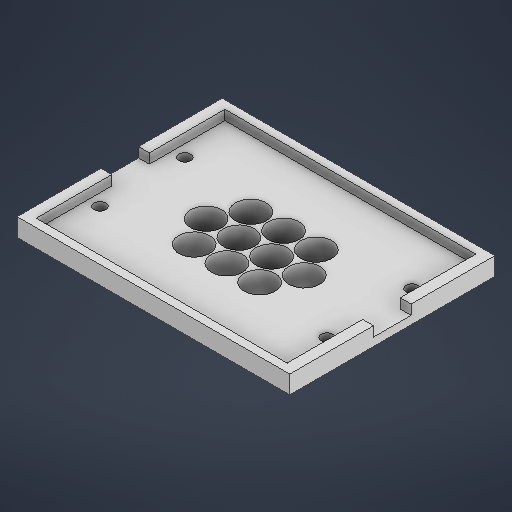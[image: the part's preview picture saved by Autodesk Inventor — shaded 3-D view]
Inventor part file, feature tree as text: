
AUTODESK INVENTOR PART (.ipt)
format: ipt  version: 2025.2 (Build 292293000, 293)  size: 641,024 bytes
history: native  units: mm
features: extrude x5, sketch x5, projected_geometry x4
ambient origin geometry x8: Origin, YZ Plane, XZ Plane, XY Plane, X Axis, Y Axis, Z Axis, Center Point
bodies: Solid1 (feature_tree)
feature tree (14):
  extrude  "Extrusion1"  Depth=19.0mm
  sketch  "Sketch4"  dims[d4=19.0mm d6=19.0mm]
  extrude  "Extrusion7"  Depth=19.0mm
  sketch  "Sketch5"  dims[d8=19.0mm d10=19.0mm]
  extrude  "Extrusion8"  Depth=19.0mm
  extrude  "Extrusion6"  Depth=19.0mm
  extrude  "Extrusion9"  Depth=15.0mm TaperAngle=0.0deg
  sketch  "Sketch1"  dims[d0=19.0mm d2=19.0mm]
  projected_geometry  "Projected Loop1"
  sketch  "Sketch6"  dims[d11=19.0mm d13=19.0mm]
  projected_geometry  "Projected Loop4"
  sketch  "Sketch7"  dims[d14=19.0mm d16=20.0mm d17=20.0mm d18=20.0mm d19=20.0mm d20=20.0mm d21=20.0mm d22=20.0mm d23=20.0mm d24=15.0mm d25=0.0mm d53=19.0mm d91=1.0mm d104=153.4mm d123=7.23mm d124=7.23mm d125=7.23mm d126=0.0mm d127=0.0mm d140=7.23mm d144=21.0mm d145=21.0mm d146=21.0mm d147=21.0mm d148=21.0mm d149=21.0mm d150=21.0mm d151=21.0mm d152=21.0mm d153=21.0mm d154=23.0mm d155=23.0mm d156=23.0mm d157=23.0mm d158=23.0mm d159=23.0mm d160=23.0mm d161=23.0mm d162=23.0mm d163=23.0mm d164=115.4mm d165=8.0mm d166=0.0mm d169=5.0mm d170=6.646447mm d171=166.692894mm d172=125.4mm d173=6.0mm d174=5.0mm d175=0.0mm d176=0.0mm d177=0.0mm d178=0.0mm d179=31.75mm d180=7.228mm d181=7.228mm d182=31.75mm d183=31.75mm d184=7.228mm d185=7.228mm d186=31.75mm]
  projected_geometry  "Projected Loop5"
  projected_geometry  "Projected Loop6"
